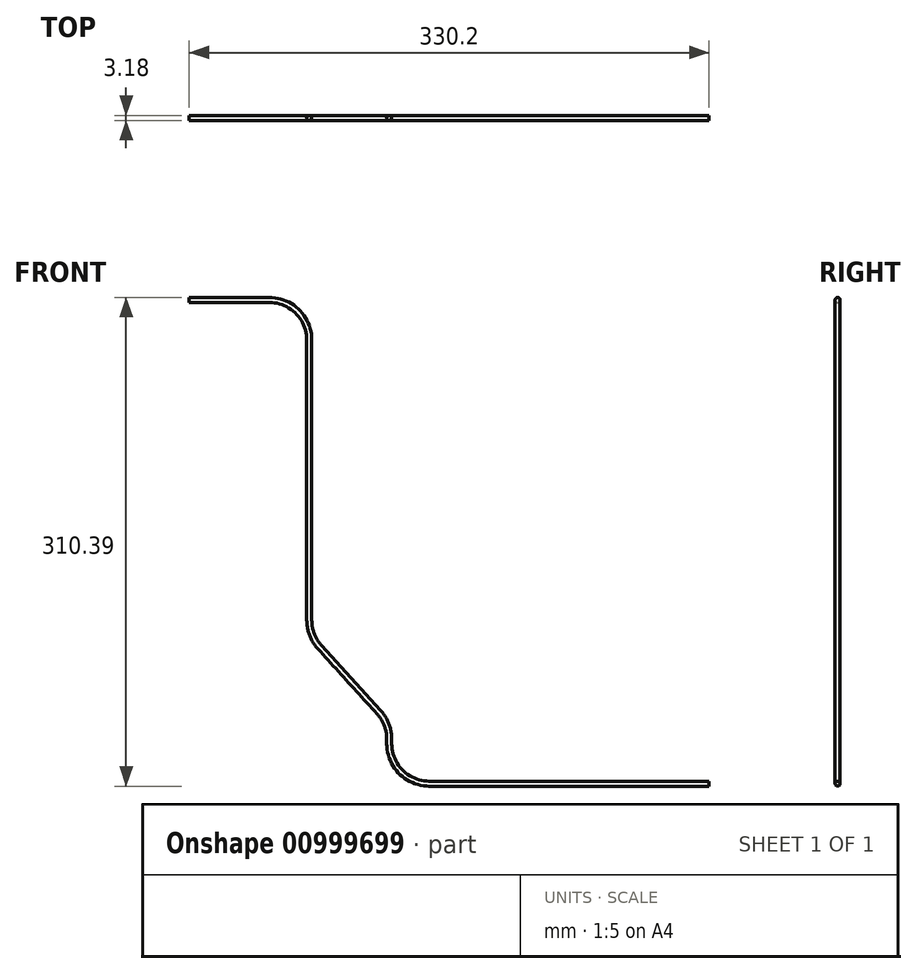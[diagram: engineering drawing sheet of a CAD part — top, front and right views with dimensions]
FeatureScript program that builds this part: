
annotation { "Feature Type Name" : "Feature", "Feature Type Description" : "" }
export const myFeature = defineFeature(function(context is Context, id is Id, definition is map)
    precondition{}
    {
        {
            var Q0;
            Q0=qCreatedBy(makeId("Front.planeOp"),FACE);
            var sketch = newSketch(context, id + "F0", { "sketchPlane" : qUnion([Q0])});
            skLineSegment(sketch, "E0", {"start": v(0, 0) * mm, "end": v(-177.8, 0) * mm});
            skLineSegment(sketch, "E1", {"start": v(-203.2, 25.4) * mm, "end": v(-203.2, 28.28) * mm});
            skLineSegment(sketch, "E2", {"start": v(-209.8, 45.37) * mm, "end": v(-247.4, 86.71) * mm});
            skLineSegment(sketch, "E3", {"start": v(-254, 103.8) * mm, "end": v(-254, 281.81) * mm});
            skLineSegment(sketch, "E4", {"start": v(-279.4, 307.21) * mm, "end": v(-330.2, 307.21) * mm});
            skPoint(sketch, "E5.visualSharp", {"position": v(-254, 307.21) * mm});
            skArc(sketch, "E5.filletArc", {"start": v(-254, 281.81) * mm, "mid": v(-261.44, 299.77) * mm, "end": v(-279.4, 307.21) * mm});
            skPoint(sketch, "E6.visualSharp", {"position": v(-254, 93.98) * mm});
            skArc(sketch, "E6.filletArc", {"start": v(-254, 103.8) * mm, "mid": v(-252.3, 94.64) * mm, "end": v(-247.4, 86.71) * mm});
            skPoint(sketch, "E7.visualSharp", {"position": v(-203.2, 38.1) * mm});
            skArc(sketch, "E7.filletArc", {"start": v(-203.2, 28.28) * mm, "mid": v(-204.9, 37.44) * mm, "end": v(-209.8, 45.37) * mm});
            skPoint(sketch, "E8.visualSharp", {"position": v(-203.2, 0) * mm});
            skArc(sketch, "E8.filletArc", {"start": v(-203.2, 25.4) * mm, "mid": v(-195.76, 7.44) * mm, "end": v(-177.8, 0) * mm});
            skSolve(sketch);
        }
        {
            var Q0;
            Q0=qCreatedBy(makeId("Right.planeOp"),FACE);
            var sketch = newSketch(context, id + "F1", { "sketchPlane" : qUnion([Q0])});
            skCircle(sketch, "E9", {"center": v(0, 0) * mm, "radius": 1.59 * mm});
            skSolve(sketch);
        }
        {
            var Q0;
            Q0=makeQuery(id+"F1.imprint","IMPRINT",FACE,{"disambiguationData":[TD([[makeQuery(id+"F1.imprint","IMPRINT",EDGE,{"derivedFrom":sQuery(id+"F1.wireOp",EDGE,"E9")}),1.0]])]});
            var Q1;
            Q1=sQuery(id+"F0.wireOp",EDGE,"E0");
            var Q2;
            Q2=sQuery(id+"F0.wireOp",EDGE,"E8.filletArc");
            var Q3;
            Q3=sQuery(id+"F0.wireOp",EDGE,"E1");
            var Q4;
            Q4=sQuery(id+"F0.wireOp",EDGE,"E7.filletArc");
            var Q5;
            Q5=sQuery(id+"F0.wireOp",EDGE,"E2");
            var Q6;
            Q6=sQuery(id+"F0.wireOp",EDGE,"E3");
            var Q7;
            Q7=sQuery(id+"F0.wireOp",EDGE,"E6.filletArc");
            var Q8;
            Q8=sQuery(id+"F0.wireOp",EDGE,"E4");
            var Q9;
            Q9=sQuery(id+"F0.wireOp",EDGE,"E5.filletArc");
            sweep(context, id + "F2", {"profiles" : qUnion([Q0]), "path" : qUnion([Q1, Q2, Q3, Q4, Q5, Q6, Q7, Q8, Q9])});
        }
    });
